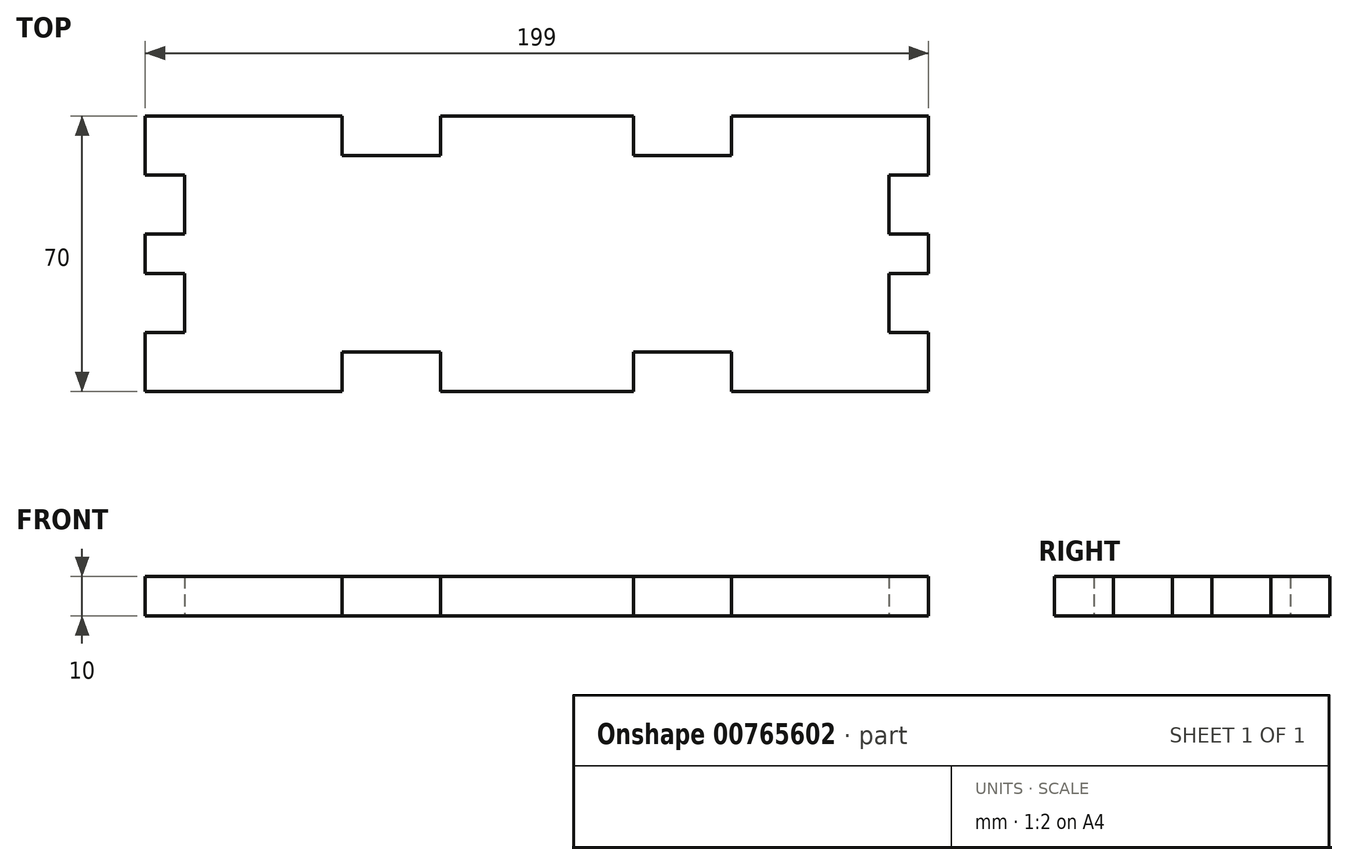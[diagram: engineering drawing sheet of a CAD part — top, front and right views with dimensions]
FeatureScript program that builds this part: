
annotation { "Feature Type Name" : "Feature", "Feature Type Description" : "" }
export const myFeature = defineFeature(function(context is Context, id is Id, definition is map)
    precondition{}
    {
        {
            var Q0;
            Q0=qCreatedBy(makeId("Top.planeOp"),FACE);
            var sketch = newSketch(context, id + "F0", { "sketchPlane" : qUnion([Q0])});
            skPoint(sketch, "E0.middle", {"position": v(0, 0) * mm});
            skLineSegment(sketch, "E1", {"start": v(-99.5, 35) * mm, "end": v(-49.5, 35) * mm});
            skLineSegment(sketch, "E2", {"start": v(-49.5, 35) * mm, "end": v(-49.5, 25) * mm});
            skLineSegment(sketch, "E3.MirrorCS", {"start": v(99.5, 35) * mm, "end": v(49.5, 35) * mm});
            skLineSegment(sketch, "E4.MirrorCS", {"start": v(49.5, 35) * mm, "end": v(49.5, 25) * mm});
            skLineSegment(sketch, "E5", {"start": v(-49.5, 25) * mm, "end": v(-24.5, 25) * mm});
            skLineSegment(sketch, "E6", {"start": v(-24.5, 25) * mm, "end": v(-24.5, 35) * mm});
            skLineSegment(sketch, "E7.MirrorCS", {"start": v(49.5, 25) * mm, "end": v(24.5, 25) * mm});
            skLineSegment(sketch, "E8.MirrorCS", {"start": v(24.5, 25) * mm, "end": v(24.5, 35) * mm});
            skLineSegment(sketch, "E9", {"start": v(-24.5, 35) * mm, "end": v(24.5, 35) * mm});
            skLineSegment(sketch, "E10", {"start": v(-99.5, -35) * mm, "end": v(-99.5, -20) * mm});
            skLineSegment(sketch, "E11", {"start": v(-99.5, -20) * mm, "end": v(-89.5, -20) * mm});
            skLineSegment(sketch, "E12.MirrorCS", {"start": v(-99.5, 35) * mm, "end": v(-99.5, 20) * mm});
            skLineSegment(sketch, "E13.MirrorCS", {"start": v(-99.5, 20) * mm, "end": v(-89.5, 20) * mm});
            skLineSegment(sketch, "E14", {"start": v(-89.5, 20) * mm, "end": v(-89.5, 5) * mm});
            skLineSegment(sketch, "E15", {"start": v(-89.5, 5) * mm, "end": v(-99.5, 5) * mm});
            skLineSegment(sketch, "E16.MirrorCS", {"start": v(-89.5, -20) * mm, "end": v(-89.5, -5) * mm});
            skLineSegment(sketch, "E17.MirrorCS", {"start": v(-89.5, -5) * mm, "end": v(-99.5, -5) * mm});
            skLineSegment(sketch, "E18", {"start": v(-99.5, -5) * mm, "end": v(-99.5, 5) * mm});
            skLineSegment(sketch, "E19.MirrorCS", {"start": v(99.5, 35) * mm, "end": v(99.5, 20) * mm});
            skLineSegment(sketch, "E20.MirrorCS", {"start": v(99.5, 20) * mm, "end": v(89.5, 20) * mm});
            skLineSegment(sketch, "E21.MirrorCS", {"start": v(89.5, 20) * mm, "end": v(89.5, 5) * mm});
            skLineSegment(sketch, "E22.MirrorCS", {"start": v(89.5, 5) * mm, "end": v(99.5, 5) * mm});
            skLineSegment(sketch, "E23.MirrorCS", {"start": v(99.5, -5) * mm, "end": v(99.5, 5) * mm});
            skLineSegment(sketch, "E24.MirrorCS", {"start": v(89.5, -5) * mm, "end": v(99.5, -5) * mm});
            skLineSegment(sketch, "E25.MirrorCS", {"start": v(89.5, -20) * mm, "end": v(89.5, -5) * mm});
            skLineSegment(sketch, "E26.MirrorCS", {"start": v(99.5, -20) * mm, "end": v(89.5, -20) * mm});
            skLineSegment(sketch, "E27.MirrorCS", {"start": v(99.5, -35) * mm, "end": v(99.5, -20) * mm});
            skLineSegment(sketch, "E28.MirrorCS", {"start": v(-49.5, -35) * mm, "end": v(-49.5, -25) * mm});
            skLineSegment(sketch, "E29.MirrorCS", {"start": v(-49.5, -25) * mm, "end": v(-24.5, -25) * mm});
            skLineSegment(sketch, "E30.MirrorCS", {"start": v(-24.5, -25) * mm, "end": v(-24.5, -35) * mm});
            skLineSegment(sketch, "E31.MirrorCS", {"start": v(24.5, -25) * mm, "end": v(24.5, -35) * mm});
            skLineSegment(sketch, "E32.MirrorCS", {"start": v(49.5, -25) * mm, "end": v(24.5, -25) * mm});
            skLineSegment(sketch, "E33.MirrorCS", {"start": v(49.5, -35) * mm, "end": v(49.5, -25) * mm});
            skLineSegment(sketch, "E34.MirrorCS", {"start": v(-99.5, -35) * mm, "end": v(-49.5, -35) * mm});
            skLineSegment(sketch, "E35.MirrorCS", {"start": v(99.5, -35) * mm, "end": v(49.5, -35) * mm});
            skLineSegment(sketch, "E36.MirrorCS", {"start": v(-24.5, -35) * mm, "end": v(24.5, -35) * mm});
            skSolve(sketch);
        }
        {
            var Q0;
            Q0=makeQuery(id+"F0.imprint","IMPRINT",FACE,{"disambiguationData":[TD([[makeQuery(id+"F0.imprint","IMPRINT",EDGE,{"derivedFrom":sQuery(id+"F0.wireOp",EDGE,"E1")}),-1.0]])]});
            extrude(context, id + "F1", {"entities" : qUnion([Q0]), "depth" : 10 * mm, "offsetDistance" : 25 * mm});
        }
    });
